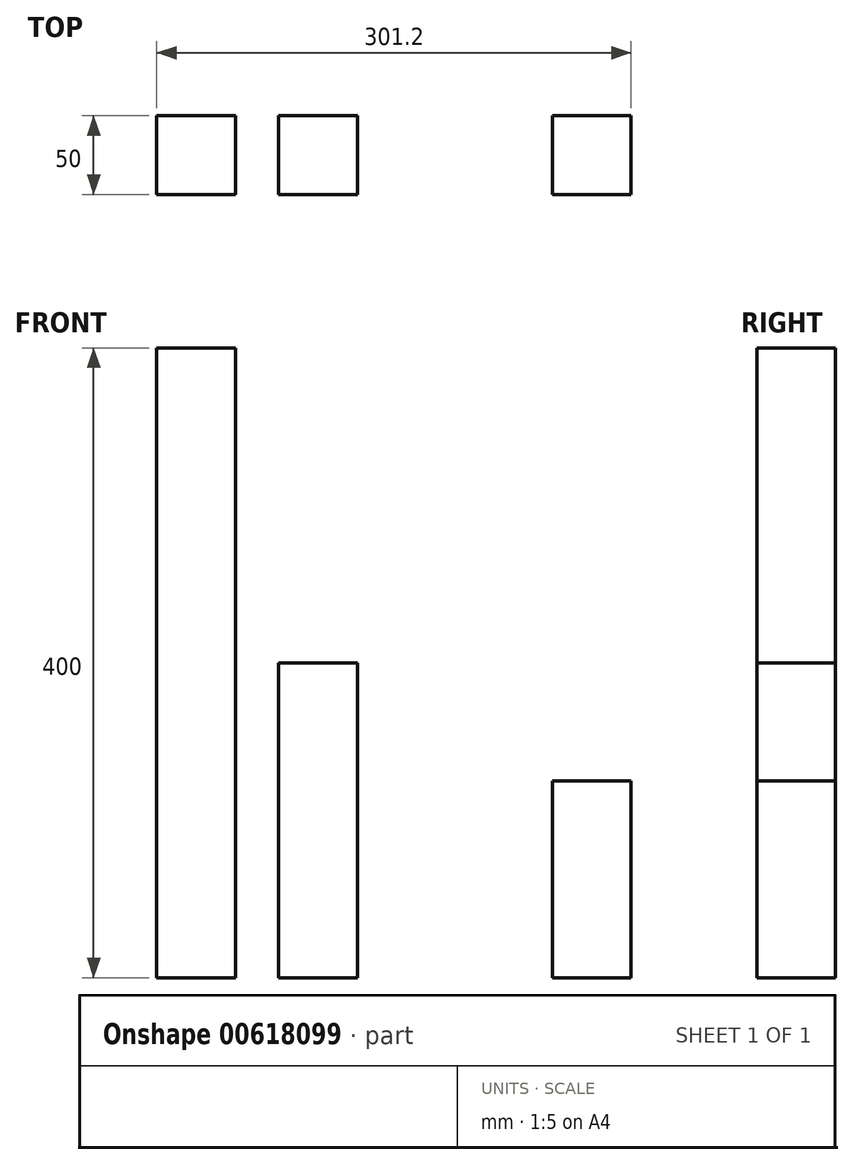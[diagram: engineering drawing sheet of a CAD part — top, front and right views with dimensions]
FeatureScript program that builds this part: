
annotation { "Feature Type Name" : "Feature", "Feature Type Description" : "" }
export const myFeature = defineFeature(function(context is Context, id is Id, definition is map)
    precondition{}
    {
        {
            var Q0;
            Q0=qCreatedBy(makeId("Front.planeOp"),FACE);
            var sketch = newSketch(context, id + "F0", { "sketchPlane" : qUnion([Q0])});
            skLineSegment(sketch, "E0.bottom", {"start": v(-52.82, 335.45) * mm, "end": v(-2.82, 335.45) * mm});
            skLineSegment(sketch, "E0.top", {"start": v(-52.82, -64.55) * mm, "end": v(-2.82, -64.55) * mm});
            skLineSegment(sketch, "E0.left", {"start": v(-52.82, 335.45) * mm, "end": v(-52.82, -64.55) * mm});
            skLineSegment(sketch, "E0.right", {"start": v(-2.82, 335.45) * mm, "end": v(-2.82, -64.55) * mm});
            skLineSegment(sketch, "E1", {"start": v(-2.82, -64.55) * mm, "end": v(100.84, -64.55) * mm, "construction": true});
            skLineSegment(sketch, "E2.bottom", {"start": v(24.6, -64.55) * mm, "end": v(74.6, -64.55) * mm});
            skLineSegment(sketch, "E2.top", {"start": v(24.6, 135.45) * mm, "end": v(74.6, 135.45) * mm});
            skLineSegment(sketch, "E2.left", {"start": v(24.6, -64.55) * mm, "end": v(24.6, 135.45) * mm});
            skLineSegment(sketch, "E2.right", {"start": v(74.6, -64.55) * mm, "end": v(74.6, 135.45) * mm});
            skLineSegment(sketch, "E3.bottom", {"start": v(198.38, -64.55) * mm, "end": v(248.38, -64.55) * mm});
            skLineSegment(sketch, "E3.top", {"start": v(198.38, 60.45) * mm, "end": v(248.38, 60.45) * mm});
            skLineSegment(sketch, "E3.left", {"start": v(198.38, -64.55) * mm, "end": v(198.38, 60.45) * mm});
            skLineSegment(sketch, "E3.right", {"start": v(248.38, -64.55) * mm, "end": v(248.38, 60.45) * mm});
            skLineSegment(sketch, "E4.trimOffspring", {"start": v(150.84, -64.55) * mm, "end": v(399.58, -64.55) * mm, "construction": true});
            skSolve(sketch);
        }
        {
            var Q0;
            Q0=makeQuery(id+"F0.imprint","IMPRINT",FACE,{"disambiguationData":[TD([[makeQuery(id+"F0.imprint","IMPRINT",EDGE,{"derivedFrom":sQuery(id+"F0.wireOp",EDGE,"E0.bottom")}),-1.0]])]});
            var Q1;
            Q1=makeQuery(id+"F0.imprint","IMPRINT",FACE,{"disambiguationData":[TD([[makeQuery(id+"F0.imprint","IMPRINT",EDGE,{"derivedFrom":sQuery(id+"F0.wireOp",EDGE,"E2.bottom")}),1.0]])]});
            var Q2;
            Q2=makeQuery(id+"F0.imprint","IMPRINT",FACE,{"disambiguationData":[TD([[makeQuery(id+"F0.imprint","IMPRINT",EDGE,{"derivedFrom":sQuery(id+"F0.wireOp",EDGE,"GQxfcmy4-J8FD-XJRk-CEyv-BHnE8mNgeHWe.bottom")}),1.0]])]});
            var Q3;
            Q3=makeQuery(id+"F0.imprint","IMPRINT",FACE,{"disambiguationData":[TD([[makeQuery(id+"F0.imprint","IMPRINT",EDGE,{"derivedFrom":sQuery(id+"F0.wireOp",EDGE,"E3.bottom")}),1.0]])]});
            extrude(context, id + "F1", {"entities" : qUnion([Q0, Q1, Q2, Q3]), "depth" : 50 * mm, "offsetDistance" : 25 * mm});
        }
    });
